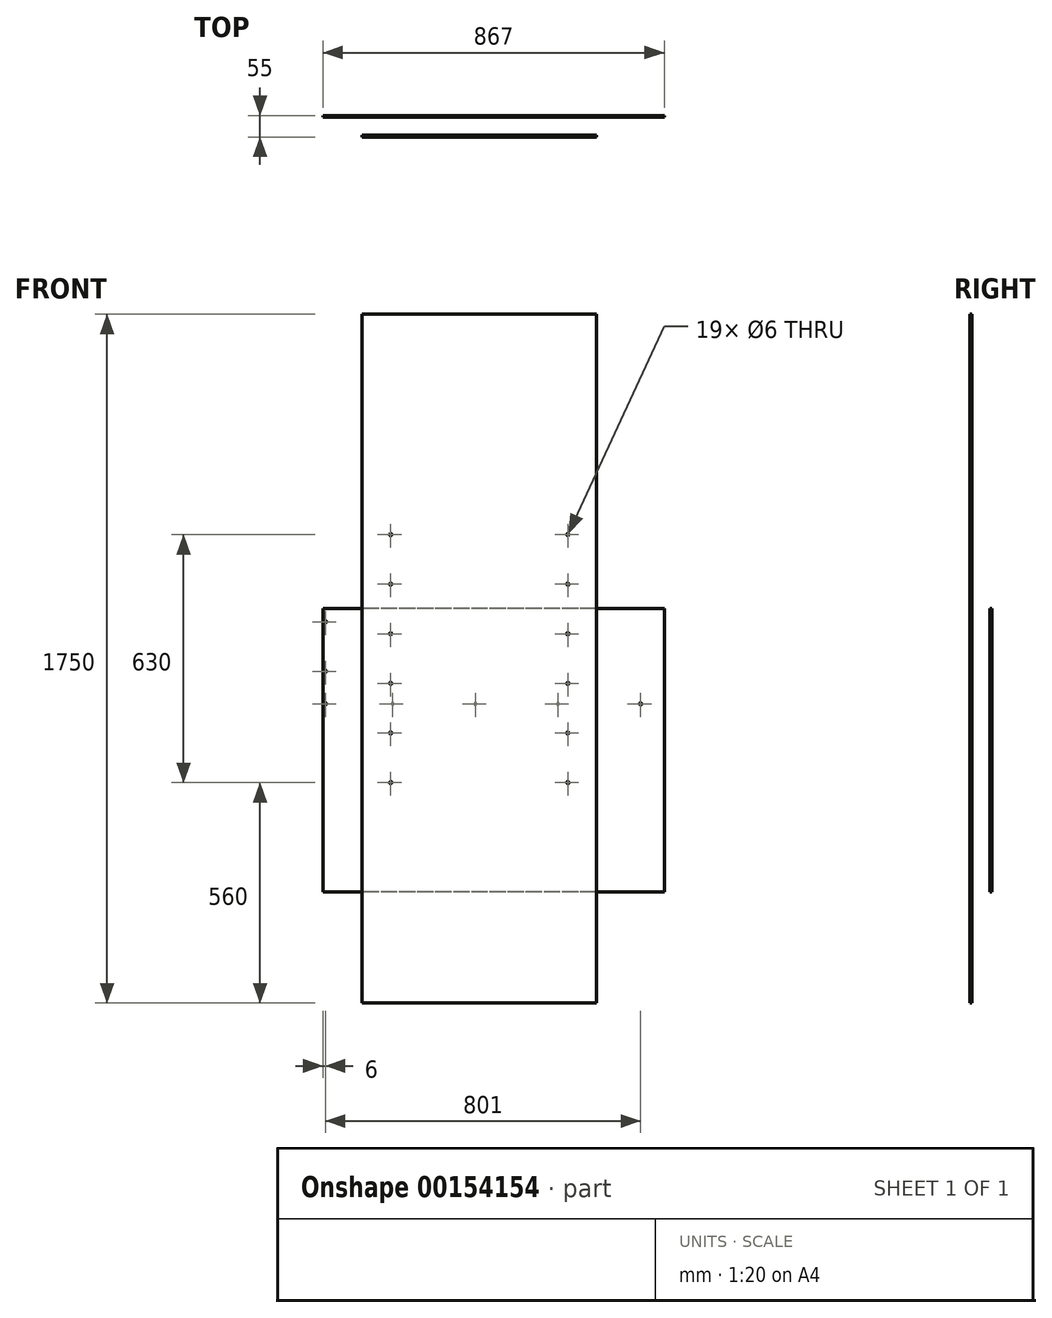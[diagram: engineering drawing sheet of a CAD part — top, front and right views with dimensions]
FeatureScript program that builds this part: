
annotation { "Feature Type Name" : "Feature", "Feature Type Description" : "" }
export const myFeature = defineFeature(function(context is Context, id is Id, definition is map)
    precondition{}
    {
        {
            var Q0;
            Q0=qCreatedBy(makeId("Front.planeOp"),FACE);
            var sketch = newSketch(context, id + "F0", { "sketchPlane" : qUnion([Q0])});
            skLineSegment(sketch, "E0.bottom", {"start": v(470, 127.5) * mm, "end": v(-397, 127.5) * mm});
            skLineSegment(sketch, "E0.top", {"start": v(470, -127.5) * mm, "end": v(-470, -127.5) * mm});
            skLineSegment(sketch, "E0.left", {"start": v(470, 127.5) * mm, "end": v(470, -127.5) * mm});
            skLineSegment(sketch, "E0.right", {"start": v(-470, 127.5) * mm, "end": v(-470, -127.5) * mm});
            skPoint(sketch, "E0.middle", {"position": v(0, 0) * mm});
            skLineSegment(sketch, "E1", {"start": v(470, -127.5) * mm, "end": v(470, -592.5) * mm});
            skLineSegment(sketch, "E2", {"start": v(470, -592.5) * mm, "end": v(-397, -592.5) * mm});
            skLineSegment(sketch, "E3", {"start": v(-470, -592.5) * mm, "end": v(-470, -127.5) * mm});
            skPoint(sketch, "E4", {"position": v(-397, 127.5) * mm});
            skLineSegment(sketch, "E5", {"start": v(-397, 127.5) * mm, "end": v(-397, -592.5) * mm});
            skSolve(sketch);
        }
        {
            var Q0;
            Q0 = qSketchRegion(id + "F0", true);
            extrude(context, id + "F1", {"entities" : qUnion([Q0]), "depth" : 5 * mm});
        }
        {
            var Q0;
            Q0=qCreatedBy(makeId("Front.planeOp"),FACE);
            cPlane(context, id + "F2", {"entities" : qUnion([Q0]), "cplaneType" : CPlaneType.OFFSET, "offset" : 50 * mm, "width" : 150 * mm, "height" : 150 * mm});
        }
        {
            var Q0;
            Q0=qCreatedBy(id+"F2.planeOp",FACE);
            var sketch = newSketch(context, id + "F3", { "sketchPlane" : qUnion([Q0])});
            skLineSegment(sketch, "E6.bottom", {"start": v(297.5, 410) * mm, "end": v(-297.5, 410) * mm});
            skLineSegment(sketch, "E6.top", {"start": v(297.5, -410) * mm, "end": v(-297.5, -410) * mm});
            skLineSegment(sketch, "E6.left", {"start": v(297.5, 410) * mm, "end": v(297.5, -410) * mm});
            skLineSegment(sketch, "E6.right", {"start": v(-297.5, 410) * mm, "end": v(-297.5, -410) * mm});
            skPoint(sketch, "E6.middle", {"position": v(0, 0) * mm});
            skSolve(sketch);
        }
        {
            var Q0;
            Q0 = qSketchRegion(id + "F3", true);
            extrude(context, id + "F4", {"entities" : qUnion([Q0]), "depth" : 5 * mm});
        }
        {
            var Q0;
            Q0=makeQuery(id+"F1.opExtrude","CAP_FACE",FACE,{"disambiguationData":[OSD([sQuery(id+"F0.wireOp",EDGE,"E0.bottom"),sQuery(id+"F0.wireOp",EDGE,"E0.top"),sQuery(id+"F0.wireOp",EDGE,"E0.left"),sQuery(id+"F0.wireOp",EDGE,"E0.right")])],"isStart":false});
            var sketch = newSketch(context, id + "F5", { "sketchPlane" : qUnion([Q0])});
            skPoint(sketch, "E7", {"position": v(410, -115) * mm});
            skPoint(sketch, "E8", {"position": v(200, -115) * mm});
            skPoint(sketch, "E9", {"position": v(-10, -115) * mm});
            skPoint(sketch, "E10", {"position": v(-220, -115) * mm});
            skCircle(sketch, "E11", {"center": v(-220, -115) * mm, "radius": 3 * mm});
            skCircle(sketch, "E12", {"center": v(-10, -115) * mm, "radius": 3 * mm});
            skCircle(sketch, "E13", {"center": v(200, -115) * mm, "radius": 3 * mm});
            skCircle(sketch, "E14", {"center": v(410, -115) * mm, "radius": 3 * mm});
            skPoint(sketch, "E15", {"position": v(-391, -32.5) * mm});
            skPoint(sketch, "E16", {"position": v(-391, 93.5) * mm});
            skCircle(sketch, "E17", {"center": v(-391, 93.5) * mm, "radius": 3 * mm});
            skCircle(sketch, "E18", {"center": v(-391, -32.5) * mm, "radius": 3 * mm});
            skLineSegment(sketch, "E19", {"start": v(-385, 127.5) * mm, "end": v(-385, -592.5) * mm});
            skPoint(sketch, "E20", {"position": v(-391, -115) * mm});
            skCircle(sketch, "E21", {"center": v(-391, -115) * mm, "radius": 3 * mm});
            skSolve(sketch);
        }
        {
            var Q0;
            Q0 = qSketchRegion(id + "F5", true);
            extrude(context, id + "F6", {"entities" : qUnion([Q0]), "operationType" : NewBodyOperationType.REMOVE, "oppositeDirection" : true, "depth" : 5 * mm});
        }
        {
            var Q0;
            Q0=makeQuery(id+"F4.opExtrude","CAP_FACE",FACE,{"disambiguationData":[OSD([sQuery(id+"F3.wireOp",EDGE,"E6.bottom"),sQuery(id+"F3.wireOp",EDGE,"E6.top"),sQuery(id+"F3.wireOp",EDGE,"E6.left"),sQuery(id+"F3.wireOp",EDGE,"E6.right")])],"isStart":false});
            var sketch = newSketch(context, id + "F7", { "sketchPlane" : qUnion([Q0])});
            skPoint(sketch, "E22", {"position": v(-225, -315) * mm});
            skPoint(sketch, "E23", {"position": v(-225, -189) * mm});
            skPoint(sketch, "E24", {"position": v(-225, -63) * mm});
            skPoint(sketch, "E25", {"position": v(-225, 63) * mm});
            skPoint(sketch, "E26", {"position": v(-225, 189) * mm});
            skPoint(sketch, "E27", {"position": v(-225, 315) * mm});
            skCircle(sketch, "E28", {"center": v(-225, -315) * mm, "radius": 3 * mm});
            skCircle(sketch, "E29", {"center": v(-225, -189) * mm, "radius": 3 * mm});
            skCircle(sketch, "E30", {"center": v(-225, -63) * mm, "radius": 3 * mm});
            skCircle(sketch, "E31", {"center": v(-225, 63) * mm, "radius": 3 * mm});
            skCircle(sketch, "E32", {"center": v(-225, 189) * mm, "radius": 3 * mm});
            skCircle(sketch, "E33", {"center": v(-225, 315) * mm, "radius": 3 * mm});
            skLineSegment(sketch, "E34", {"start": v(0, 0) * mm, "end": v(0, -150) * mm});
            skCircle(sketch, "E35.MirrorC", {"center": v(225, 315) * mm, "radius": 3 * mm});
            skCircle(sketch, "E36.MirrorC", {"center": v(225, 189) * mm, "radius": 3 * mm});
            skCircle(sketch, "E37.MirrorC", {"center": v(225, 63) * mm, "radius": 3 * mm});
            skCircle(sketch, "E38.MirrorC", {"center": v(225, -63) * mm, "radius": 3 * mm});
            skCircle(sketch, "E39.MirrorC", {"center": v(225, -189) * mm, "radius": 3 * mm});
            skCircle(sketch, "E40.MirrorC", {"center": v(225, -315) * mm, "radius": 3 * mm});
            skSolve(sketch);
        }
        {
            var Q0;
            Q0 = qSketchRegion(id + "F7", true);
            extrude(context, id + "F8", {"entities" : qUnion([Q0]), "operationType" : NewBodyOperationType.REMOVE, "oppositeDirection" : true, "depth" : 25 * mm});
        }
        {
            var Q0;
            Q0=makeQuery(id+"F4.opExtrude","CAP_FACE",FACE,{"disambiguationData":[OSD([sQuery(id+"F3.wireOp",EDGE,"E6.bottom"),sQuery(id+"F3.wireOp",EDGE,"E6.top"),sQuery(id+"F3.wireOp",EDGE,"E6.left"),sQuery(id+"F3.wireOp",EDGE,"E6.right")])],"isStart":true});
            var sketch = newSketch(context, id + "F9", { "sketchPlane" : qUnion([Q0])});
            skLineSegment(sketch, "E41", {"start": v(-297.5, -410) * mm, "end": v(-297.5, -875) * mm});
            skLineSegment(sketch, "E42", {"start": v(-297.5, -875) * mm, "end": v(297.5, -875) * mm});
            skLineSegment(sketch, "E43", {"start": v(297.5, -875) * mm, "end": v(297.5, -410) * mm});
            skLineSegment(sketch, "E44", {"start": v(297.5, -410) * mm, "end": v(-297.5, -410) * mm});
            skLineSegment(sketch, "E45", {"start": v(-297.5, 410) * mm, "end": v(-297.5, 875) * mm});
            skLineSegment(sketch, "E46", {"start": v(-297.5, 875) * mm, "end": v(297.5, 875) * mm});
            skLineSegment(sketch, "E47", {"start": v(297.5, 875) * mm, "end": v(297.5, 410) * mm});
            skSolve(sketch);
        }
        {
            var Q0;
            Q0 = qSketchRegion(id + "F9", true);
            var Q1;
            Q1=makeQuery(id+"F9.imprint","IMPRINT",FACE,{"disambiguationData":[TD([[makeQuery(id+"F9.imprint","IMPRINT",EDGE,{"derivedFrom":sQuery(id+"F9.wireOp",EDGE,"E45")}),-1.0]])]});
            extrude(context, id + "F10", {"entities" : qUnion([Q0, Q1]), "operationType" : NewBodyOperationType.ADD, "oppositeDirection" : true, "depth" : 5 * mm});
        }
    });
